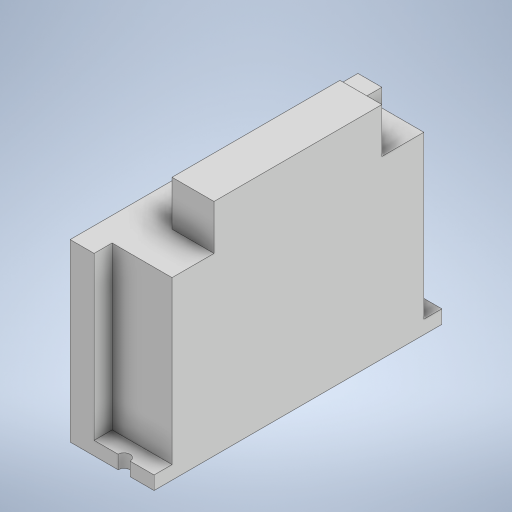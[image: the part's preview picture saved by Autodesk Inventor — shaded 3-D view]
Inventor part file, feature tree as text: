
AUTODESK INVENTOR PART (.ipt)
format: ipt  version: 2024 (Build 280153000, 153)  size: 253,440 bytes
history: native  units: mm
features: extrude x4, sketch x4, projected_geometry x4
ambient origin geometry x8: Origin, YZ Plane, XZ Plane, XY Plane, X Axis, Y Axis, Z Axis, Center Point
bodies: Body1 (feature_tree)
feature tree (12):
  extrude  "Extrusion3"  Depth=96.0mm
  extrude  "Extrusion4"  Depth=8.0mm
  extrude  "Extrusion5"  Depth=6.0mm
  extrude  "Extrusion6"  Depth=15.0mm
  sketch  "Sketch3"  dims[d6=28.0mm d7=96.0mm]
  sketch  "Sketch4"  dims[d8=4.5mm d9=0.0mm d10=8.0mm]
  projected_geometry  "Projected Loop1"
  sketch  "Sketch5"  dims[d11=6.0mm d12=6.0mm]
  projected_geometry  "Projected Loop2"
  projected_geometry  "Projected Loop3"
  sketch  "Sketch6"  dims[d13=54.0mm d14=0.0mm d15=4.0mm d16=4.0mm d17=0.0mm d18=0.0mm d19=14.0mm d21=14.0mm d22=14.0mm d23=15.0mm d24=0.0mm]
  projected_geometry  "Projected Loop4"
